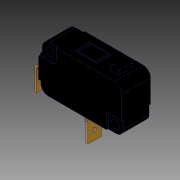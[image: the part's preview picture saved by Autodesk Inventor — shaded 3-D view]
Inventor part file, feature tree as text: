
AUTODESK INVENTOR PART (.ipt)
format: ipt  version: 2018 (Build 220112000, 112)  size: 244,736 bytes
history: native  units: in
note: dims shown in document units (in); Inventor stores cm internally (conversion verified against a paired STEP export)
features: extrude x3, sketch x3, mirror x2, plane x1, fillet x1
ambient origin geometry x8: Origin, YZ Plane, XZ Plane, XY Plane, X Axis, Y Axis, Z Axis, Center Point
bodies: Solid1 (feature_tree)
feature tree (10):
  extrude  "Extrusion1"  Depth=0.0197in
  plane  "Work Plane1"
  mirror  "Mirror1"
  extrude  "Extrusion2"  Depth=0.0472in
  mirror  "Mirror2"
  extrude  "Extrusion4"  Depth=0.0197in TaperAngle=0.0deg
  sketch  "Sketch1"  dims[d1=0.0197in d2=0.0in d5=0.0472in]
  sketch  "Sketch2"  dims[d6=0.0472in d7=0.0472in]
  sketch  "Sketch3"  dims[d8=0.0472in d9=0.0197in d10=0.0in d12=0.1969in d15=0.0079in d16=0.0079in d17=0.0394in d18=0.0197in d19=0.0in]
  fillet  "Fillet1"  Radius=0.1969in
